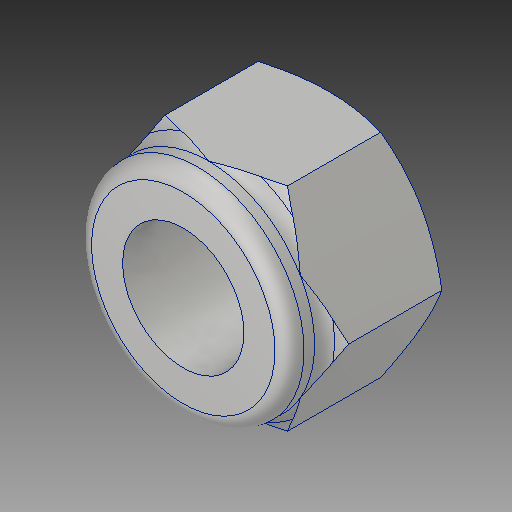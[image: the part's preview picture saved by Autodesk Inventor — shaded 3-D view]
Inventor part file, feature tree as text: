
AUTODESK INVENTOR PART (.ipt)
format: ipt  version: 2017 (Build 210142000, 142)  size: 188,416 bytes
history: native  units: in
note: dims shown in document units (in); Inventor stores cm internally (conversion verified against a paired STEP export)
features: fillet x1
ambient origin geometry x8: Origin, YZ Plane, XZ Plane, XY Plane, X Axis, Y Axis, Z Axis, Center Point
bodies: Solid1 (feature_tree)
feature tree (1):
  fillet  "Fillet7"  [1 undecoded]
note: 1 required parameter value undecoded (feature->parameter linkage not recoverable at this tier; creation-order binding heuristic only, values carry confidence <= 0.55)
